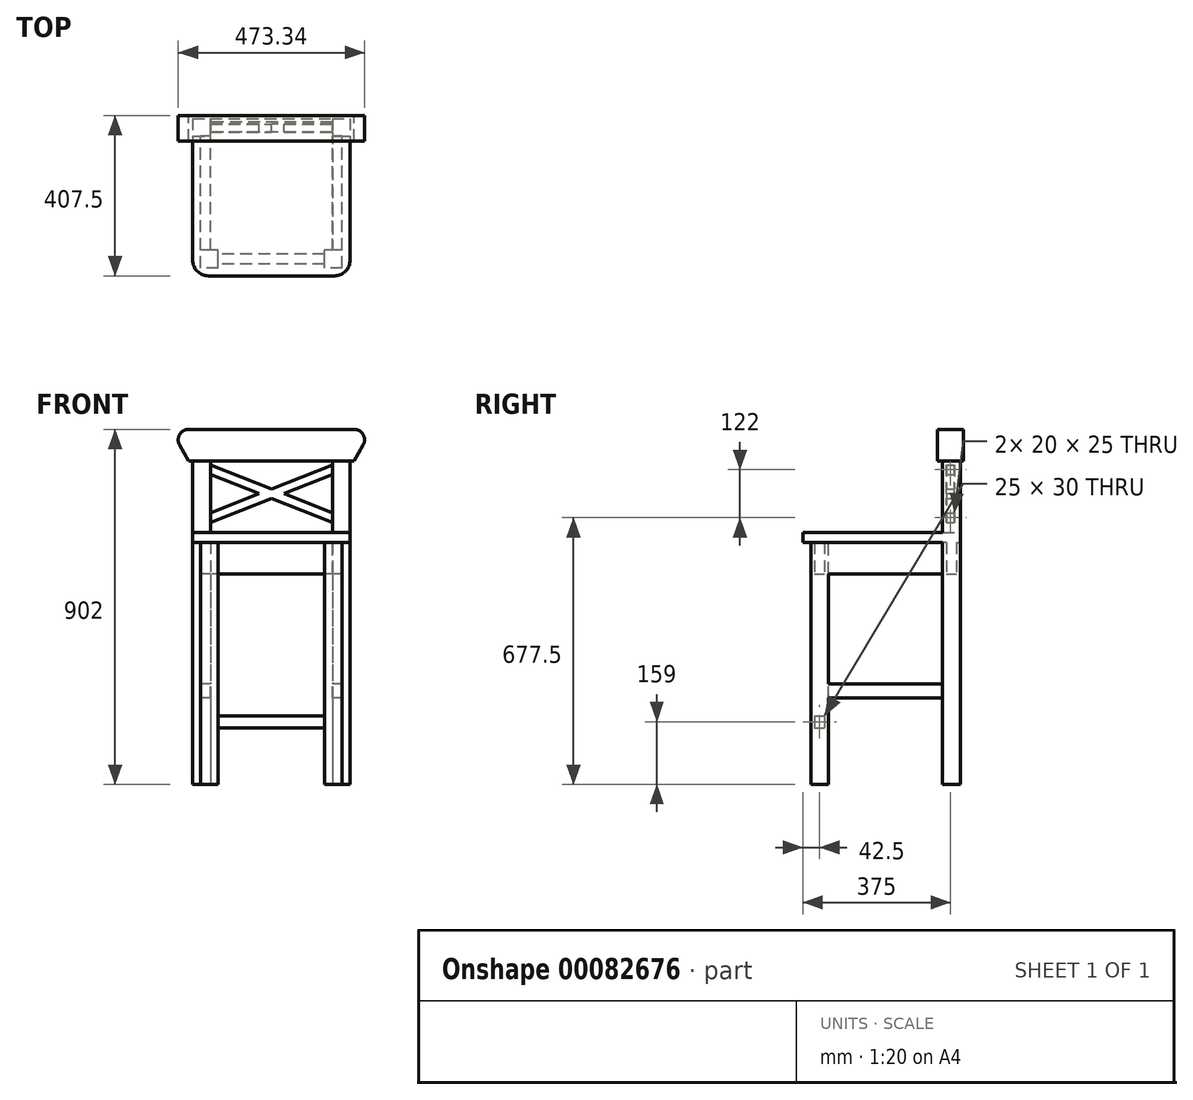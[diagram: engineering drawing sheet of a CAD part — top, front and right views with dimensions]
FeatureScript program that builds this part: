
annotation { "Feature Type Name" : "Feature", "Feature Type Description" : "" }
export const myFeature = defineFeature(function(context is Context, id is Id, definition is map)
    precondition{}
    {
        {
            var Q0;
            Q0=qCreatedBy(makeId("Top.planeOp"),FACE);
            var sketch = newSketch(context, id + "F0", { "sketchPlane" : qUnion([Q0])});
            skLineSegment(sketch, "E0.bottom", {"start": v(-155, 200) * mm, "end": v(155, 200) * mm});
            skLineSegment(sketch, "E0.top", {"start": v(-160, -200) * mm, "end": v(160, -200) * mm});
            skLineSegment(sketch, "E0.left", {"start": v(-200, 155) * mm, "end": v(-200, -160) * mm});
            skLineSegment(sketch, "E0.right", {"start": v(200, 155) * mm, "end": v(200, -160) * mm});
            skLineSegment(sketch, "E1", {"start": v(-200, 0) * mm, "end": v(200, 0) * mm, "construction": true});
            skLineSegment(sketch, "E2", {"start": v(-200, 155) * mm, "end": v(-155, 155) * mm});
            skLineSegment(sketch, "E3", {"start": v(-155, 155) * mm, "end": v(-155, 200) * mm});
            skLineSegment(sketch, "E4", {"start": v(155, 200) * mm, "end": v(155, 155) * mm});
            skLineSegment(sketch, "E5", {"start": v(155, 155) * mm, "end": v(200, 155) * mm});
            skPoint(sketch, "E6.visualSharp", {"position": v(-200, -200) * mm});
            skArc(sketch, "E6.filletArc", {"start": v(-200, -160) * mm, "mid": v(-188.28, -188.28) * mm, "end": v(-160, -200) * mm});
            skPoint(sketch, "E7.visualSharp", {"position": v(200, -200) * mm});
            skArc(sketch, "E7.filletArc", {"start": v(160, -200) * mm, "mid": v(188.28, -188.28) * mm, "end": v(200, -160) * mm});
            skPoint(sketch, "E8.orphan", {"position": v(-200, 200) * mm});
            skPoint(sketch, "E9.orphan", {"position": v(200, 200) * mm});
            skSolve(sketch);
        }
        {
            var Q0;
            Q0 = qSketchRegion(id + "F0", true);
            extrude(context, id + "F1", {"entities" : qUnion([Q0]), "depth" : 25 * mm});
        }
        {
            var Q0;
            Q0=qCreatedBy(makeId("Top.planeOp"),FACE);
            var sketch = newSketch(context, id + "F2", { "sketchPlane" : qUnion([Q0])});
            skLineSegment(sketch, "E10.bottom", {"start": v(180, -180) * mm, "end": v(135, -180) * mm});
            skLineSegment(sketch, "E10.top", {"start": v(180, -135) * mm, "end": v(135, -135) * mm});
            skLineSegment(sketch, "E10.left", {"start": v(180, -180) * mm, "end": v(180, -135) * mm});
            skLineSegment(sketch, "E10.right", {"start": v(135, -180) * mm, "end": v(135, -135) * mm});
            skLineSegment(sketch, "E11.bottom", {"start": v(-135, -180) * mm, "end": v(-180, -180) * mm});
            skLineSegment(sketch, "E11.top", {"start": v(-135, -135) * mm, "end": v(-180, -135) * mm});
            skLineSegment(sketch, "E11.left", {"start": v(-135, -180) * mm, "end": v(-135, -135) * mm});
            skLineSegment(sketch, "E11.right", {"start": v(-180, -180) * mm, "end": v(-180, -135) * mm});
            skSolve(sketch);
        }
        {
            var Q0;
            Q0 = qSketchRegion(id + "F2", true);
            extrude(context, id + "F3", {"entities" : qUnion([Q0]), "operationType" : NewBodyOperationType.ADD, "oppositeDirection" : true, "depth" : 615 * mm});
        }
        {
            var Q0;
            Q0=qCreatedBy(makeId("Top.planeOp"),FACE);
            var sketch = newSketch(context, id + "F4", { "sketchPlane" : qUnion([Q0])});
            skLineSegment(sketch, "E12.bottom", {"start": v(-200, 200) * mm, "end": v(-155, 200) * mm});
            skLineSegment(sketch, "E12.top", {"start": v(-200, 155) * mm, "end": v(-155, 155) * mm});
            skLineSegment(sketch, "E12.left", {"start": v(-200, 200) * mm, "end": v(-200, 155) * mm});
            skLineSegment(sketch, "E12.right", {"start": v(-155, 200) * mm, "end": v(-155, 155) * mm});
            skLineSegment(sketch, "E13.bottom", {"start": v(155, 200) * mm, "end": v(200, 200) * mm});
            skLineSegment(sketch, "E13.top", {"start": v(155, 155) * mm, "end": v(200, 155) * mm});
            skLineSegment(sketch, "E13.left", {"start": v(155, 200) * mm, "end": v(155, 155) * mm});
            skLineSegment(sketch, "E13.right", {"start": v(200, 200) * mm, "end": v(200, 155) * mm});
            skSolve(sketch);
        }
        {
            var Q0;
            Q0 = qSketchRegion(id + "F4", true);
            extrude(context, id + "F5", {"entities" : qUnion([Q0]), "operationType" : NewBodyOperationType.ADD, "depth" : 287 * mm, "hasSecondDirection" : true, "secondDirectionOppositeDirection" : true, "secondDirectionDepth" : 615 * mm});
        }
        {
            var Q0;
            Q0=qCreatedBy(makeId("Front.planeOp"),FACE);
            var sketch = newSketch(context, id + "F6", { "sketchPlane" : qUnion([Q0])});
            skLineSegment(sketch, "E14.bottom", {"start": v(-180, 0) * mm, "end": v(-155, 0) * mm});
            skLineSegment(sketch, "E14.top", {"start": v(-180, -80) * mm, "end": v(-155, -80) * mm});
            skLineSegment(sketch, "E14.left", {"start": v(-180, 0) * mm, "end": v(-180, -80) * mm});
            skLineSegment(sketch, "E14.right", {"start": v(-155, 0) * mm, "end": v(-155, -80) * mm});
            skLineSegment(sketch, "E15.bottom", {"start": v(155, 0) * mm, "end": v(180, 0) * mm});
            skLineSegment(sketch, "E15.top", {"start": v(155, -80) * mm, "end": v(180, -80) * mm});
            skLineSegment(sketch, "E15.left", {"start": v(155, 0) * mm, "end": v(155, -80) * mm});
            skLineSegment(sketch, "E15.right", {"start": v(180, 0) * mm, "end": v(180, -80) * mm});
            skLineSegment(sketch, "E16.bottom", {"start": v(-180, -360) * mm, "end": v(-155, -360) * mm});
            skLineSegment(sketch, "E16.top", {"start": v(-180, -396) * mm, "end": v(-155, -396) * mm});
            skLineSegment(sketch, "E16.left", {"start": v(-180, -360) * mm, "end": v(-180, -396) * mm});
            skLineSegment(sketch, "E16.right", {"start": v(-155, -360) * mm, "end": v(-155, -396) * mm});
            skLineSegment(sketch, "E17.bottom", {"start": v(155, -360) * mm, "end": v(180, -360) * mm});
            skLineSegment(sketch, "E17.top", {"start": v(155, -396) * mm, "end": v(180, -396) * mm});
            skLineSegment(sketch, "E17.left", {"start": v(155, -360) * mm, "end": v(155, -396) * mm});
            skLineSegment(sketch, "E17.right", {"start": v(180, -360) * mm, "end": v(180, -396) * mm});
            skSolve(sketch);
        }
        {
            var Q0;
            Q0 = qSketchRegion(id + "F6", true);
            extrude(context, id + "F7", {"entities" : qUnion([Q0]), "operationType" : NewBodyOperationType.ADD, "endBound" : BoundingType.UP_TO_NEXT, "depth" : 400 * mm, "hasSecondDirection" : true, "secondDirectionBound" : SecondDirectionBoundingType.UP_TO_NEXT, "secondDirectionOppositeDirection" : true, "secondDirectionDepth" : 25 * mm});
        }
        {
            var Q0;
            Q0=qCreatedBy(makeId("Right.planeOp"),FACE);
            var sketch = newSketch(context, id + "F8", { "sketchPlane" : qUnion([Q0])});
            skLineSegment(sketch, "E18.bottom", {"start": v(-170, 0) * mm, "end": v(-145, 0) * mm});
            skLineSegment(sketch, "E18.top", {"start": v(-170, -80) * mm, "end": v(-145, -80) * mm});
            skLineSegment(sketch, "E18.left", {"start": v(-170, 0) * mm, "end": v(-170, -80) * mm});
            skLineSegment(sketch, "E18.right", {"start": v(-145, 0) * mm, "end": v(-145, -80) * mm});
            skLineSegment(sketch, "E19.bottom", {"start": v(165, 0) * mm, "end": v(190, 0) * mm});
            skLineSegment(sketch, "E19.top", {"start": v(165, -80) * mm, "end": v(190, -80) * mm});
            skLineSegment(sketch, "E19.left", {"start": v(165, 0) * mm, "end": v(165, -80) * mm});
            skLineSegment(sketch, "E19.right", {"start": v(190, 0) * mm, "end": v(190, -80) * mm});
            skLineSegment(sketch, "E20.bottom", {"start": v(-170, -441) * mm, "end": v(-145, -441) * mm});
            skLineSegment(sketch, "E20.top", {"start": v(-170, -471) * mm, "end": v(-145, -471) * mm});
            skLineSegment(sketch, "E20.left", {"start": v(-170, -441) * mm, "end": v(-170, -471) * mm});
            skLineSegment(sketch, "E20.right", {"start": v(-145, -441) * mm, "end": v(-145, -471) * mm});
            skSolve(sketch);
        }
        {
            var Q0;
            Q0 = qSketchRegion(id + "F8", true);
            extrude(context, id + "F9", {"entities" : qUnion([Q0]), "operationType" : NewBodyOperationType.ADD, "endBound" : BoundingType.UP_TO_NEXT, "depth" : 25 * mm, "hasSecondDirection" : true, "secondDirectionBound" : SecondDirectionBoundingType.UP_TO_NEXT, "secondDirectionOppositeDirection" : true, "secondDirectionDepth" : 25 * mm});
        }
        {
            var Q0;
            Q0=qCreatedBy(makeId("Front.planeOp"),FACE);
            cPlane(context, id + "F10", {"entities" : qUnion([Q0]), "cplaneType" : CPlaneType.OFFSET, "offset" : 175 * mm, "oppositeDirection" : true, "width" : 150 * mm, "height" : 150 * mm});
        }
        {
            var Q0;
            Q0=qCreatedBy(id+"F10.planeOp",FACE);
            var sketch = newSketch(context, id + "F11", { "sketchPlane" : qUnion([Q0])});
            skLineSegment(sketch, "E21", {"start": v(-210, 287) * mm, "end": v(210, 287) * mm});
            skLineSegment(sketch, "E22", {"start": v(-210, 207) * mm, "end": v(210, 207) * mm});
            skLineSegment(sketch, "E23", {"start": v(210, 207) * mm, "end": v(233.1, 247) * mm});
            skLineSegment(sketch, "E24", {"start": v(-210, 207) * mm, "end": v(-233.1, 247) * mm});
            skLineSegment(sketch, "E25", {"start": v(210, 287) * mm, "end": v(210, 207) * mm, "construction": true});
            skLineSegment(sketch, "E26", {"start": v(-233.1, 247) * mm, "end": v(233.1, 247) * mm, "construction": true});
            skArc(sketch, "E27", {"start": v(-210, 287) * mm, "mid": v(-233.1, 273.67) * mm, "end": v(-233.1, 247) * mm});
            skLineSegment(sketch, "E28", {"start": v(-210, 287) * mm, "end": v(-210, 207) * mm, "construction": true});
            skArc(sketch, "E29", {"start": v(210, 287) * mm, "mid": v(233.1, 273.67) * mm, "end": v(233.1, 247) * mm});
            skSolve(sketch);
        }
        {
            var Q0;
            Q0 = qSketchRegion(id + "F11", true);
            extrude(context, id + "F12", {"entities" : qUnion([Q0]), "operationType" : NewBodyOperationType.ADD, "endBound" : BoundingType.SYMMETRIC, "depth" : 65 * mm});
        }
        {
            var Q0;
            Q0=qCreatedBy(id+"F10.planeOp",FACE);
            var sketch = newSketch(context, id + "F13", { "sketchPlane" : qUnion([Q0])});
            skLineSegment(sketch, "E30.bottom", {"start": v(-155, 197) * mm, "end": v(155, 197) * mm, "construction": true});
            skLineSegment(sketch, "E30.top", {"start": v(-155, 50) * mm, "end": v(155, 50) * mm, "construction": true});
            skLineSegment(sketch, "E30.left", {"start": v(-155, 197) * mm, "end": v(-155, 50) * mm, "construction": true});
            skLineSegment(sketch, "E30.right", {"start": v(155, 197) * mm, "end": v(155, 50) * mm, "construction": true});
            skLineSegment(sketch, "E31", {"start": v(-155, 50) * mm, "end": v(155, 172) * mm});
            skLineSegment(sketch, "E32", {"start": v(155, 172) * mm, "end": v(155, 197) * mm});
            skLineSegment(sketch, "E33", {"start": v(155, 197) * mm, "end": v(-155, 75) * mm});
            skLineSegment(sketch, "E34", {"start": v(-155, 75) * mm, "end": v(-155, 50) * mm});
            skLineSegment(sketch, "E35", {"start": v(155, 50) * mm, "end": v(-155, 172) * mm});
            skLineSegment(sketch, "E36", {"start": v(-155, 172) * mm, "end": v(-155, 197) * mm});
            skLineSegment(sketch, "E37", {"start": v(-155, 197) * mm, "end": v(155, 75) * mm});
            skLineSegment(sketch, "E38", {"start": v(155, 75) * mm, "end": v(155, 50) * mm});
            skSolve(sketch);
        }
        {
            var Q0;
            Q0 = qSketchRegion(id + "F13", true);
            extrude(context, id + "F14", {"entities" : qUnion([Q0]), "operationType" : NewBodyOperationType.ADD, "endBound" : BoundingType.SYMMETRIC, "depth" : 20 * mm});
        }
    });
